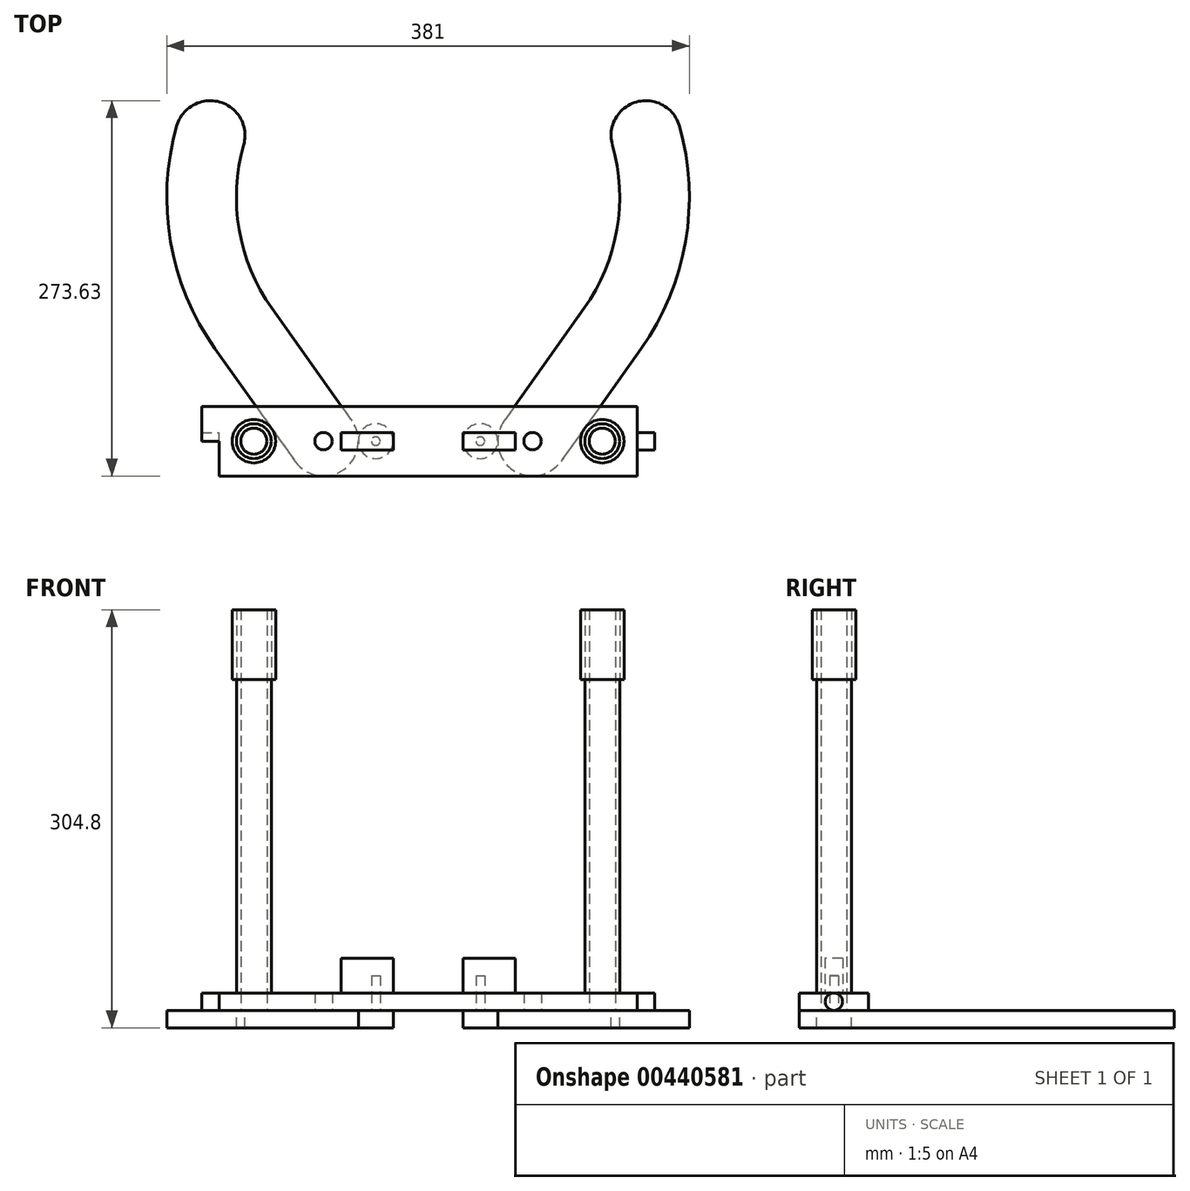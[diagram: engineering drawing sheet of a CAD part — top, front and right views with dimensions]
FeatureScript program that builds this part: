
annotation { "Feature Type Name" : "Feature", "Feature Type Description" : "" }
export const myFeature = defineFeature(function(context is Context, id is Id, definition is map)
    precondition{}
    {
        {
            var Q0;
            Q0=qCreatedBy(makeId("Top.planeOp"),FACE);
            var sketch = newSketch(context, id + "F0", { "sketchPlane" : qUnion([Q0])});
            skLineSegment(sketch, "E0.bottom", {"start": v(-152.4, 0) * mm, "end": v(152.4, 0) * mm});
            skLineSegment(sketch, "E0.top", {"start": v(-152.4, 50.8) * mm, "end": v(152.4, 50.8) * mm});
            skLineSegment(sketch, "E0.left", {"start": v(-152.4, 0) * mm, "end": v(-152.4, 50.8) * mm});
            skLineSegment(sketch, "E0.right", {"start": v(152.4, 0) * mm, "end": v(152.4, 50.8) * mm});
            skPoint(sketch, "E0.middle", {"position": v(0, 25.4) * mm});
            skCircle(sketch, "E1", {"center": v(-127, 25.4) * mm, "radius": 9.53 * mm});
            skCircle(sketch, "E2", {"center": v(127, 25.4) * mm, "radius": 9.53 * mm});
            skSolve(sketch);
        }
        {
            var Q0;
            Q0=makeQuery(id+"F0.imprint","IMPRINT",FACE,{"disambiguationData":[TD([[makeQuery(id+"F0.imprint","IMPRINT",EDGE,{"derivedFrom":sQuery(id+"F0.wireOp",EDGE,"E0.bottom")}),1.0]])]});
            extrude(context, id + "F1", {"entities" : qUnion([Q0]), "depth" : 12.7 * mm});
        }
        {
            var Q0;
            Q0=makeQuery(id+"F1.opExtrude","CAP_FACE",FACE,{"disambiguationData":[OSD([sQuery(id+"F0.wireOp",EDGE,"E0.bottom"),sQuery(id+"F0.wireOp",EDGE,"E0.top"),sQuery(id+"F0.wireOp",EDGE,"E0.left"),sQuery(id+"F0.wireOp",EDGE,"E0.right"),sQuery(id+"F0.wireOp",EDGE,"E1"),sQuery(id+"F0.wireOp",EDGE,"E2")])],"isStart":false});
            var sketch = newSketch(context, id + "F2", { "sketchPlane" : qUnion([Q0])});
            skCircle(sketch, "E3", {"center": v(-127, 25.4) * mm, "radius": 12.7 * mm});
            skCircle(sketch, "E4", {"center": v(127, 25.4) * mm, "radius": 12.7 * mm});
            skSolve(sketch);
        }
        {
            var Q0;
            Q0=makeQuery(id+"F2.imprint","IMPRINT",FACE,{"disambiguationData":[TD([[makeQuery(id+"F2.imprint","IMPRINT",EDGE,{"derivedFrom":sQuery(id+"F2.wireOp",EDGE,"E3")}),1.0]])]});
            var Q1;
            Q1=makeQuery(id+"F2.imprint","IMPRINT",FACE,{"disambiguationData":[TD([[makeQuery(id+"F2.imprint","IMPRINT",EDGE,{"derivedFrom":sQuery(id+"F2.wireOp",EDGE,"E4")}),1.0]])]});
            extrude(context, id + "F3", {"entities" : qUnion([Q0, Q1]), "depth" : 279.4 * mm});
        }
        {
            var Q0;
            Q0=makeQuery(id+"F1.opExtrude","CAP_FACE",FACE,{"disambiguationData":[OSD([sQuery(id+"F0.wireOp",EDGE,"E0.bottom"),sQuery(id+"F0.wireOp",EDGE,"E0.top"),sQuery(id+"F0.wireOp",EDGE,"E0.left"),sQuery(id+"F0.wireOp",EDGE,"E0.right"),sQuery(id+"F0.wireOp",EDGE,"E1"),sQuery(id+"F0.wireOp",EDGE,"E2")])],"isStart":false});
            var sketch = newSketch(context, id + "F4", { "sketchPlane" : qUnion([Q0])});
            skLineSegment(sketch, "E5.bottom", {"start": v(-25.4, 31.75) * mm, "end": v(-63.5, 31.75) * mm});
            skLineSegment(sketch, "E5.top", {"start": v(-25.4, 19.05) * mm, "end": v(-63.5, 19.05) * mm});
            skLineSegment(sketch, "E5.left", {"start": v(-25.4, 31.75) * mm, "end": v(-25.4, 19.05) * mm});
            skLineSegment(sketch, "E5.right", {"start": v(-63.5, 31.75) * mm, "end": v(-63.5, 19.05) * mm});
            skPoint(sketch, "E5.middle", {"position": v(-44.45, 25.4) * mm});
            skLineSegment(sketch, "E6.bottom", {"start": v(25.4, 31.75) * mm, "end": v(63.5, 31.75) * mm});
            skLineSegment(sketch, "E6.top", {"start": v(25.4, 19.05) * mm, "end": v(63.5, 19.05) * mm});
            skLineSegment(sketch, "E6.left", {"start": v(25.4, 31.75) * mm, "end": v(25.4, 19.05) * mm});
            skLineSegment(sketch, "E6.right", {"start": v(63.5, 31.75) * mm, "end": v(63.5, 19.05) * mm});
            skPoint(sketch, "E6.middle", {"position": v(44.45, 25.4) * mm});
            skLineSegment(sketch, "E7", {"start": v(-44.45, 25.4) * mm, "end": v(-44.45, 0) * mm, "construction": true});
            skLineSegment(sketch, "E8", {"start": v(-44.45, 25.4) * mm, "end": v(-44.45, 50.8) * mm, "construction": true});
            skPoint(sketch, "E8.endSnap0", {"position": v(-44.45, 31.75) * mm});
            skLineSegment(sketch, "E9", {"start": v(-44.45, 25.4) * mm, "end": v(0, 25.4) * mm, "construction": true});
            skLineSegment(sketch, "E10", {"start": v(44.45, 25.4) * mm, "end": v(0, 25.4) * mm, "construction": true});
            skSolve(sketch);
        }
        {
            var Q0;
            Q0=makeQuery(id+"F4.imprint","IMPRINT",FACE,{"disambiguationData":[TD([[makeQuery(id+"F4.imprint","IMPRINT",EDGE,{"derivedFrom":sQuery(id+"F4.wireOp",EDGE,"E6.bottom")}),-1.0]])]});
            var Q1;
            Q1=makeQuery(id+"F4.imprint","IMPRINT",FACE,{"disambiguationData":[TD([[makeQuery(id+"F4.imprint","IMPRINT",EDGE,{"derivedFrom":sQuery(id+"F4.wireOp",EDGE,"E5.bottom")}),1.0]])]});
            extrude(context, id + "F5", {"entities" : qUnion([Q0, Q1]), "depth" : 25.4 * mm});
        }
        {
            var Q0;
            Q0=makeQuery(id+"F1.opExtrude","CAP_FACE",FACE,{"disambiguationData":[OSD([sQuery(id+"F0.wireOp",EDGE,"E0.bottom"),sQuery(id+"F0.wireOp",EDGE,"E0.top"),sQuery(id+"F0.wireOp",EDGE,"E0.left"),sQuery(id+"F0.wireOp",EDGE,"E0.right"),sQuery(id+"F0.wireOp",EDGE,"E1"),sQuery(id+"F0.wireOp",EDGE,"E2")])],"isStart":true});
            var sketch = newSketch(context, id + "F6", { "sketchPlane" : qUnion([Q0])});
            skCircle(sketch, "E11", {"center": v(-38.1, -25.4) * mm, "radius": 3.18 * mm});
            skCircle(sketch, "E12", {"center": v(38.1, -25.4) * mm, "radius": 3.18 * mm});
            skCircle(sketch, "E13", {"center": v(-76.2, -25.4) * mm, "radius": 6.35 * mm});
            skCircle(sketch, "E14", {"center": v(76.2, -25.4) * mm, "radius": 6.35 * mm});
            skLineSegment(sketch, "E15", {"start": v(-38.1, -25.4) * mm, "end": v(-38.1, -50.8) * mm, "construction": true});
            skLineSegment(sketch, "E16", {"start": v(-38.1, -25.4) * mm, "end": v(-38.1, 0) * mm, "construction": true});
            skLineSegment(sketch, "E17", {"start": v(38.1, -25.4) * mm, "end": v(0, -25.4) * mm, "construction": true});
            skLineSegment(sketch, "E18", {"start": v(-38.1, -25.4) * mm, "end": v(0, -25.4) * mm, "construction": true});
            skLineSegment(sketch, "E19", {"start": v(-38.1, -25.4) * mm, "end": v(-76.2, -25.4) * mm, "construction": true});
            skLineSegment(sketch, "E20", {"start": v(38.1, -25.4) * mm, "end": v(76.2, -25.4) * mm, "construction": true});
            skSolve(sketch);
        }
        {
            var Q0;
            Q0 = qSketchRegion(id + "F6", true);
            extrude(context, id + "F7", {"entities" : qUnion([Q0]), "operationType" : NewBodyOperationType.REMOVE, "oppositeDirection" : true, "depth" : 25.4 * mm});
        }
        {
            var Q0;
            Q0=makeQuery(id+"F6.imprint","IMPRINT",FACE,{"disambiguationData":[TD([[makeQuery(id+"F6.imprint","IMPRINT",EDGE,{"derivedFrom":sQuery(id+"F6.wireOp",EDGE,"E11")}),-1.0]])]});
            var sketch = newSketch(context, id + "F8", { "sketchPlane" : qUnion([Q0])});
            skArc(sketch, "E21", {"start": v(-55.5, -40.11) * mm, "mid": v(-61.49, -4.7) * mm, "end": v(-96.9, -10.69) * mm});
            skCircle(sketch, "E22", {"center": v(-38.1, -25.4) * mm, "radius": 12.7 * mm});
            skCircle(sketch, "E23", {"center": v(38.1, -25.4) * mm, "radius": 12.7 * mm});
            skArc(sketch, "E24", {"start": v(96.9, -10.69) * mm, "mid": v(61.49, -4.7) * mm, "end": v(55.5, -40.11) * mm});
            skCircle(sketch, "E25", {"center": v(0, -203.2) * mm, "radius": 139.7 * mm, "construction": true});
            skArc(sketch, "E26", {"start": v(-134.4, -241.3) * mm, "mid": v(-137.67, -179.46) * mm, "end": v(-113.88, -122.28) * mm});
            skArc(sketch, "E27", {"start": v(134.4, -241.3) * mm, "mid": v(137.67, -179.46) * mm, "end": v(113.88, -122.28) * mm});
            skLineSegment(sketch, "E28", {"start": v(113.88, -122.28) * mm, "end": v(55.5, -40.11) * mm});
            skArc(sketch, "E29", {"start": v(183.28, -255.15) * mm, "mid": v(187.73, -170.83) * mm, "end": v(155.3, -92.86) * mm});
            skArc(sketch, "E30", {"start": v(-183.28, -255.15) * mm, "mid": v(-187.73, -170.83) * mm, "end": v(-155.3, -92.86) * mm});
            skLineSegment(sketch, "E31", {"start": v(-113.88, -122.28) * mm, "end": v(-55.5, -40.11) * mm});
            skLineSegment(sketch, "E32", {"start": v(155.3, -92.86) * mm, "end": v(96.9, -10.69) * mm});
            skLineSegment(sketch, "E33", {"start": v(-155.3, -92.86) * mm, "end": v(-96.9, -10.69) * mm});
            skLineSegment(sketch, "E34", {"start": v(183.28, -255.15) * mm, "end": v(134.4, -241.3) * mm, "construction": true});
            skLineSegment(sketch, "E35", {"start": v(-134.4, -241.3) * mm, "end": v(-183.28, -255.15) * mm, "construction": true});
            skArc(sketch, "E36", {"start": v(-183.28, -255.15) * mm, "mid": v(-151.91, -272.66) * mm, "end": v(-134.4, -241.3) * mm});
            skArc(sketch, "E37", {"start": v(134.4, -241.3) * mm, "mid": v(151.91, -272.66) * mm, "end": v(183.28, -255.15) * mm});
            skSolve(sketch);
        }
        {
            var Q0;
            Q0 = qSketchRegion(id + "F8", true);
            extrude(context, id + "F9", {"entities" : qUnion([Q0]), "depth" : 12.7 * mm});
        }
        {
            var Q0;
            Q0=makeQuery(id+"F3.opExtrude","CAP_FACE",FACE,{"disambiguationData":[OSD([sQuery(id+"F0.wireOp",EDGE,"E1"),sQuery(id+"F2.wireOp",EDGE,"E3")])],"isStart":false});
            var sketch = newSketch(context, id + "F10", { "sketchPlane" : qUnion([Q0])});
            skCircle(sketch, "E38", {"center": v(127, 25.4) * mm, "radius": 15.88 * mm});
            skCircle(sketch, "E39", {"center": v(-127, 25.4) * mm, "radius": 15.88 * mm});
            skCircle(sketch, "E40.0.0", {"center": v(127, 25.4) * mm, "radius": 9.53 * mm, "construction": true});
            skSolve(sketch);
        }
        {
            var Q0;
            Q0=makeQuery(id+"F10.imprint","IMPRINT",FACE,{"disambiguationData":[TD([[makeQuery(id+"F10.imprint","IMPRINT",EDGE,{"derivedFrom":sQuery(id+"F10.wireOp",EDGE,"E39")}),1.0]])]});
            var Q1;
            Q1=makeQuery(id+"F10.imprint","IMPRINT",FACE,{"disambiguationData":[TD([[makeQuery(id+"F10.imprint","IMPRINT",EDGE,{"derivedFrom":sQuery(id+"F10.wireOp",EDGE,"E38")}),1.0]])]});
            extrude(context, id + "F11", {"entities" : qUnion([Q0, Q1]), "oppositeDirection" : true, "depth" : 50.8 * mm});
        }
        {
            var Q0;
            Q0=makeQuery(id+"F1.opExtrude","SWEPT_FACE",FACE,{"disambiguationData":[OSD([sQuery(id+"F0.wireOp",EDGE,"E0.right")])]});
            var sketch = newSketch(context, id + "F12", { "sketchPlane" : qUnion([Q0])});
            skCircle(sketch, "E41", {"center": v(25.4, 6.35) * mm, "radius": 6.35 * mm});
            skSolve(sketch);
        }
        {
            var Q0;
            Q0=makeQuery(id+"F1.opExtrude","SWEPT_FACE",FACE,{"disambiguationData":[OSD([sQuery(id+"F0.wireOp",EDGE,"E0.left")])]});
            var sketch = newSketch(context, id + "F13", { "sketchPlane" : qUnion([Q0])});
            skCircle(sketch, "E42.0", {"center": v(-25.4, 6.35) * mm, "radius": 6.35 * mm});
            skSolve(sketch);
        }
        {
            var Q0;
            {var subQ0=sQuery(id+"F12.wireOp",EDGE,"E41");var subQ1=sQuery(id+"F0.wireOp",EDGE,"E0.right");var subQ2=makeQuery(id+"F12.imprint","INTERSECT",VERTEX,{"derivedFrom":[makeQuery(id+"F1.opExtrude","CAP_EDGE",EDGE,{"disambiguationData":[OSD([subQ1])],"isStart":true}),subQ0]});Q0=makeQuery(id+"F12.imprint","IMPRINT",FACE,{"disambiguationData":[TD([[makeQuery(id+"F12.imprint","IMPRINT",EDGE,{"disambiguationData":[TD([[subQ2,1.0]])],"derivedFrom":subQ0}),1.0]])]});}
            extrude(context, id + "F14", {"entities" : qUnion([Q0]), "operationType" : NewBodyOperationType.ADD, "depth" : 12.7 * mm});
        }
        {
            var Q0;
            {var subQ0=sQuery(id+"F13.wireOp",EDGE,"E42.0");var subQ1=sQuery(id+"F0.wireOp",EDGE,"E0.left");var subQ2=makeQuery(id+"F13.imprint","INTERSECT",VERTEX,{"derivedFrom":[makeQuery(id+"F1.opExtrude","CAP_EDGE",EDGE,{"disambiguationData":[OSD([subQ1])],"isStart":true}),subQ0]});Q0=makeQuery(id+"F13.imprint","IMPRINT",FACE,{"disambiguationData":[TD([[makeQuery(id+"F13.imprint","IMPRINT",EDGE,{"disambiguationData":[TD([[subQ2,1.0]])],"derivedFrom":subQ0}),-1.0]])]});}
            extrude(context, id + "F15", {"entities" : qUnion([Q0]), "operationType" : NewBodyOperationType.ADD, "depth" : 12.7 * mm});
        }
    });
